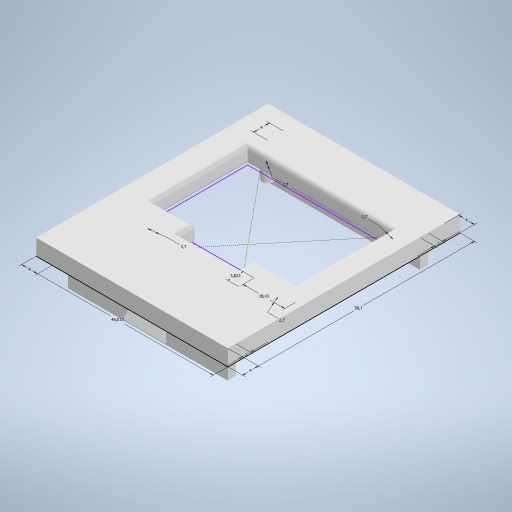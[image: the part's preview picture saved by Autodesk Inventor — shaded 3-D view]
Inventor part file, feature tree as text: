
AUTODESK INVENTOR PART (.ipt)
format: ipt  version: 2024 (Build 280153000, 153)  size: 325,632 bytes
history: native  units: mm
features: extrude x7, sketch x3, chamfer x2, fillet x1
ambient origin geometry x8: Origin, YZ Plane, XZ Plane, XY Plane, X Axis, Y Axis, Z Axis, Center Point
bodies: Volumenkörper1 (feature_tree)
feature tree (13):
  sketch  "Skizze1"  dims[d0=48.013mm d1=58.1mm]
  extrude  "Extrusion1"  Depth=58.1mm
  extrude  "Extrusion2"  Depth=4.0mm
  chamfer  "Fasen1"  Distance=4.0mm
  extrude  "Extrusion3"  Depth=2.0mm
  chamfer  "Fasen2"  Distance=2.0mm
  extrude  "Extrusion4"  Depth=7.0mm TaperAngle=0.0deg
  extrude  "Extrusion5"  Depth=3.0mm
  extrude  "Extrusion6"  Depth=3.0mm
  fillet  "Rundung1"  Radius=9.0mm
  extrude  "Extrusion7"  Depth=3.0mm
  sketch  "Skizze2"  dims[d2=4.0mm d3=4.0mm]
  sketch  "Skizze3"  dims[d4=4.0mm d5=4.0mm d6=2.0mm d7=2.0mm d8=7.0mm d9=0.0mm d10=20.0mm d11=5.0mm d12=9.0mm d13=3.6mm d14=1.8mm d15=0.0mm d16=1.8mm d17=2.0mm d18=45.0deg d19=20.0mm d20=5.0mm d21=9.0mm d22=3.6mm d23=1.8mm d24=0.0mm d25=1.8mm d26=2.0mm d27=45.0deg d28=2.7mm d29=2.7mm d30=2.7mm d31=2.7mm d32=10.43mm d33=3.822mm d34=4.0mm d35=0.0mm d36=3.0mm d37=0.0mm d38=4.0mm d39=0.0mm d40=1.0mm d41=3.0mm d42=0.0mm]
